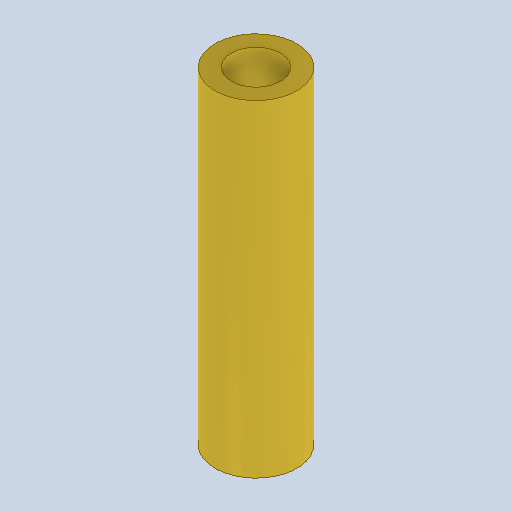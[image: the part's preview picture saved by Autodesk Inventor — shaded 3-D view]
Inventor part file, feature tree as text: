
AUTODESK INVENTOR PART (.ipt)
format: ipt  version: 2023 (Build 270158000, 158)  size: 229,376 bytes
history: native  units: in
note: dims shown in document units (in); Inventor stores cm internally (conversion verified against a paired STEP export)
features: extrude x1, sketch x1
ambient origin geometry x8: Origin, YZ Plane, XZ Plane, XY Plane, X Axis, Y Axis, Z Axis, Center Point
bodies: Solid1 (feature_tree)
feature tree (2):
  extrude  "Extrusion1"  Depth=0.7874in
  sketch  "Sketch1"  dims[d0=0.1969in d1=0.1181in d2=0.7874in d3=0.0in]
